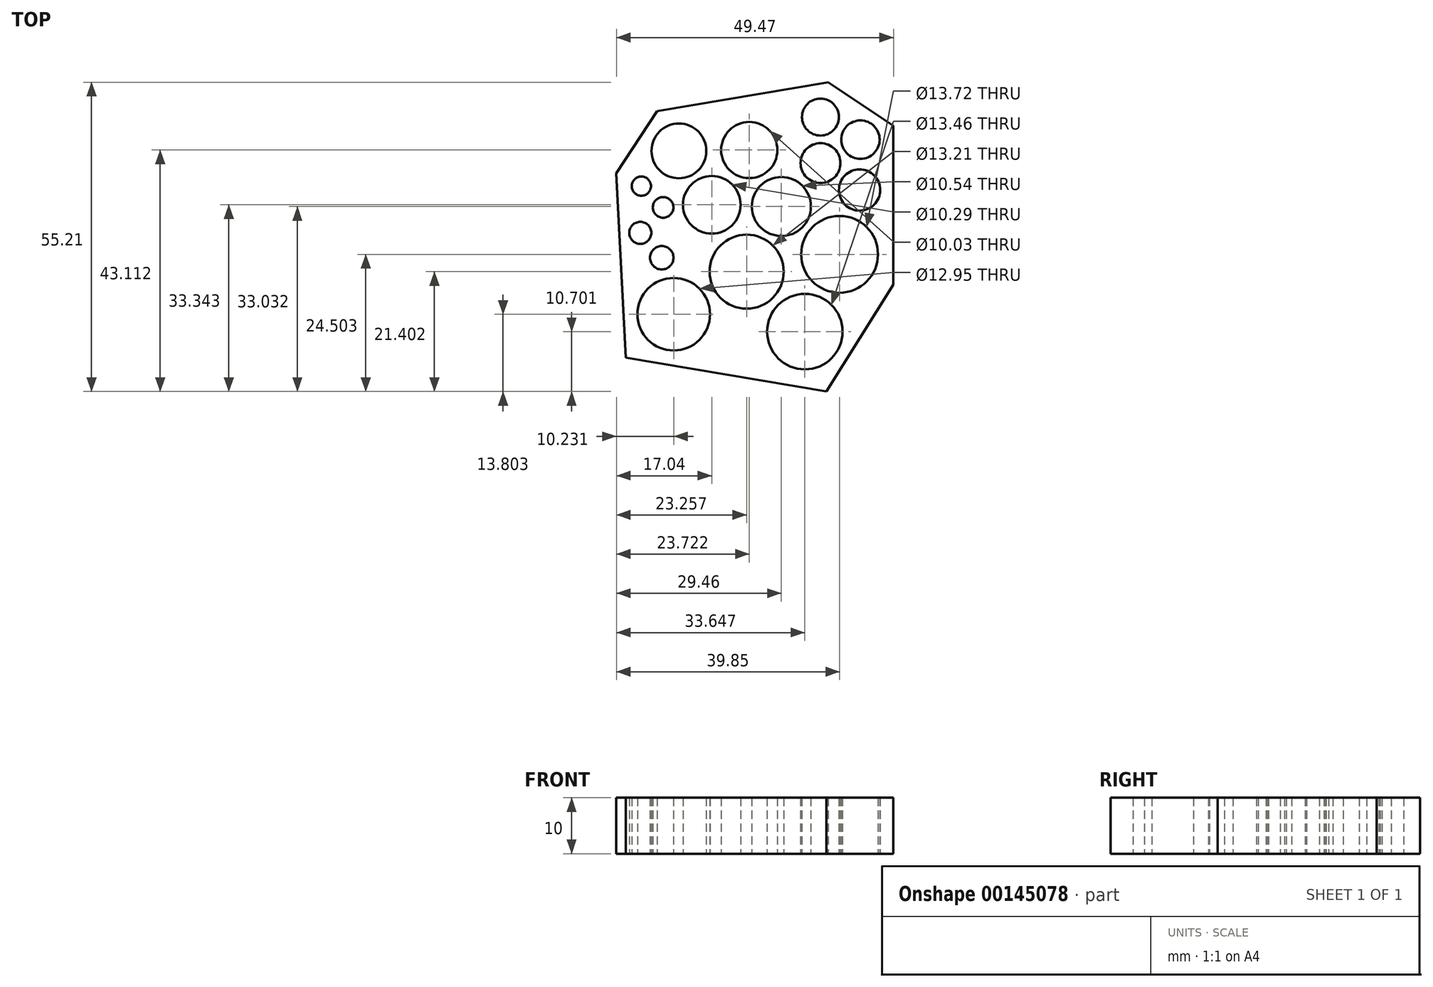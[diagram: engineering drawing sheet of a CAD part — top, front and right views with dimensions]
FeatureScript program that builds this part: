
annotation { "Feature Type Name" : "Feature", "Feature Type Description" : "" }
export const myFeature = defineFeature(function(context is Context, id is Id, definition is map)
    precondition{}
    {
        {
            var Q0;
            Q0=qCreatedBy(makeId("Top.planeOp"),FACE);
            var sketch = newSketch(context, id + "F0", { "sketchPlane" : qUnion([Q0])});
            skCircle(sketch, "E0", {"center": v(-8.7, 10.64) * mm, "radius": 1.84 * mm});
            skCircle(sketch, "E1", {"center": v(-12.77, 6.1) * mm, "radius": 1.97 * mm});
            skCircle(sketch, "E2", {"center": v(-8.94, 1.65) * mm, "radius": 2.1 * mm});
            skCircle(sketch, "E3", {"center": v(-12.59, 14.44) * mm, "radius": 1.71 * mm});
            skCircle(sketch, "E4", {"center": v(-5.88, 20.72) * mm, "radius": 4.89 * mm});
            skCircle(sketch, "E5", {"center": v(6.68, 20.87) * mm, "radius": 5.02 * mm});
            skCircle(sketch, "E6", {"center": v(0, 11.1) * mm, "radius": 5.14 * mm});
            skCircle(sketch, "E7", {"center": v(12.42, 10.8) * mm, "radius": 5.27 * mm});
            skCircle(sketch, "E8", {"center": v(19.4, 26.77) * mm, "radius": 3.3 * mm});
            skCircle(sketch, "E9", {"center": v(26.53, 22.73) * mm, "radius": 3.43 * mm});
            skCircle(sketch, "E10", {"center": v(19.4, 18.55) * mm, "radius": 3.56 * mm});
            skCircle(sketch, "E11", {"center": v(26.38, 13.74) * mm, "radius": 3.68 * mm});
            skCircle(sketch, "E12", {"center": v(6.22, -0.84) * mm, "radius": 6.6 * mm});
            skCircle(sketch, "E13", {"center": v(16.6, -11.54) * mm, "radius": 6.73 * mm});
            skCircle(sketch, "E14", {"center": v(22.81, 2.26) * mm, "radius": 6.86 * mm});
            skCircle(sketch, "E15", {"center": v(-6.8, -8.44) * mm, "radius": 6.48 * mm});
            skLineSegment(sketch, "E16", {"start": v(-17.04, 16.69) * mm, "end": v(-9.76, 27.85) * mm});
            skLineSegment(sketch, "E17", {"start": v(-9.76, 27.85) * mm, "end": v(20.8, 32.97) * mm});
            skLineSegment(sketch, "E18", {"start": v(20.8, 32.97) * mm, "end": v(32.43, 25.21) * mm});
            skLineSegment(sketch, "E19", {"start": v(32.43, 25.21) * mm, "end": v(32.43, -3.16) * mm});
            skLineSegment(sketch, "E20", {"start": v(32.43, -3.16) * mm, "end": v(20.48, -22.24) * mm});
            skLineSegment(sketch, "E21", {"start": v(20.48, -22.24) * mm, "end": v(-15.34, -16.2) * mm});
            skLineSegment(sketch, "E22", {"start": v(-15.34, -16.2) * mm, "end": v(-17.04, 16.69) * mm});
            skSolve(sketch);
        }
        {
            var Q0;
            Q0 = qSketchRegion(id + "F0", true);
            extrude(context, id + "F1", {"entities" : qUnion([Q0]), "depth" : 10 * mm});
        }
    });
